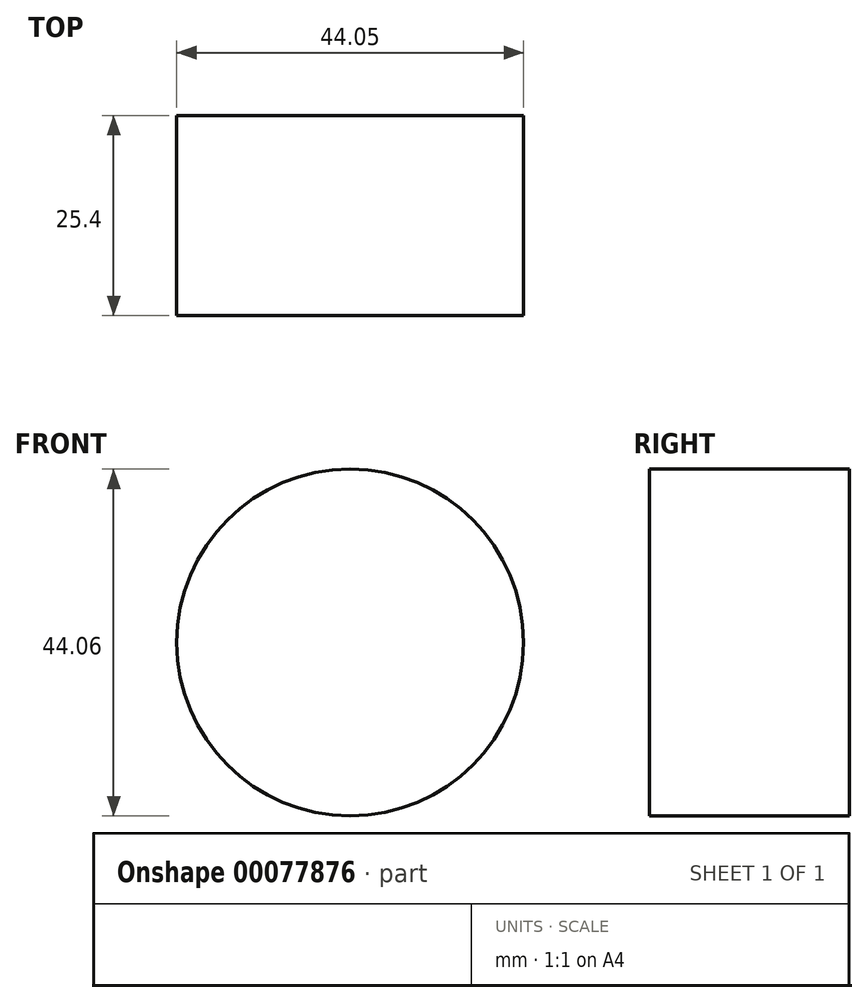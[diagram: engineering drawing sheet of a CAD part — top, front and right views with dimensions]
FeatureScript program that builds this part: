
annotation { "Feature Type Name" : "Feature", "Feature Type Description" : "" }
export const myFeature = defineFeature(function(context is Context, id is Id, definition is map)
    precondition{}
    {
        {
            var Q0;
            Q0=qCreatedBy(makeId("Front.planeOp"),FACE);
            var sketch = newSketch(context, id + "F0", { "sketchPlane" : qUnion([Q0])});
            skCircle(sketch, "E0", {"center": v(-44.92, 51.8) * mm, "radius": 22.03 * mm});
            skSolve(sketch);
        }
        {
            var Q0;
            Q0=makeQuery(id+"F0.imprint","IMPRINT",FACE,{"disambiguationData":[TD([[makeQuery(id+"F0.imprint","IMPRINT",EDGE,{"derivedFrom":sQuery(id+"F0.wireOp",EDGE,"E0")}),1.0]])]});
            extrude(context, id + "F1", {"entities" : qUnion([Q0]), "depth" : 25.4 * mm});
        }
    });
